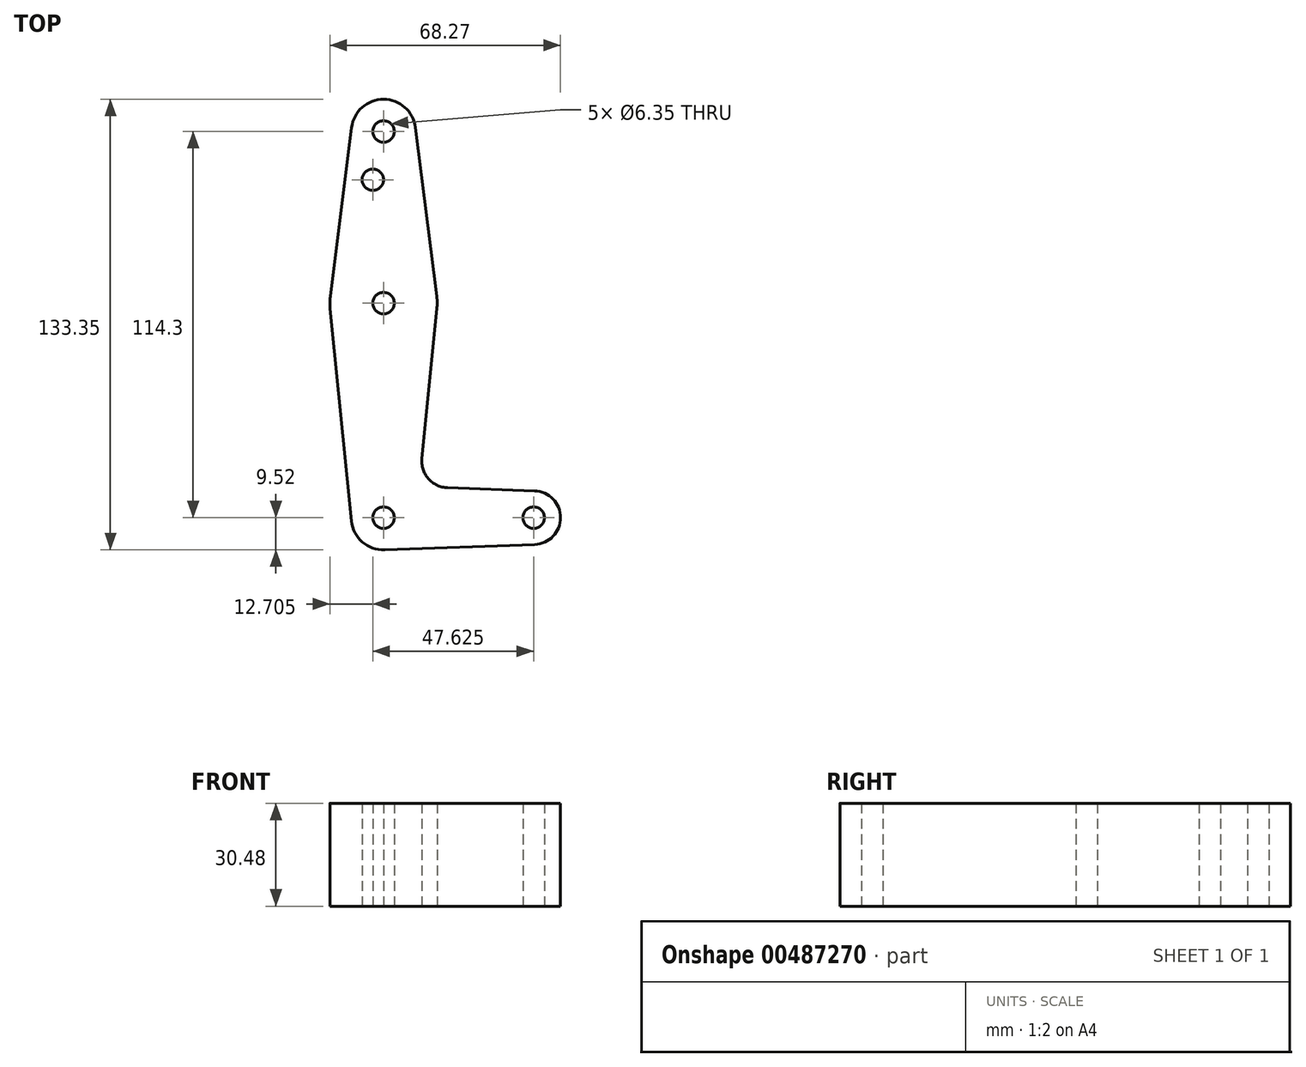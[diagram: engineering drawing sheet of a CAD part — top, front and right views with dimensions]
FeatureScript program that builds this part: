
annotation { "Feature Type Name" : "Feature", "Feature Type Description" : "" }
export const myFeature = defineFeature(function(context is Context, id is Id, definition is map)
    precondition{}
    {
        {
            var Q0;
            Q0=qCreatedBy(makeId("Top.planeOp"),FACE);
            var sketch = newSketch(context, id + "F0", { "sketchPlane" : qUnion([Q0])});
            skLineSegment(sketch, "E0", {"start": v(0, 0) * mm, "end": v(0, 114.3) * mm, "construction": true});
            skLineSegment(sketch, "E1", {"start": v(0, 0) * mm, "end": v(44.45, 0) * mm, "construction": true});
            skCircle(sketch, "E2", {"center": v(0, 114.3) * mm, "radius": 9.52 * mm});
            skCircle(sketch, "E3", {"center": v(0, 0) * mm, "radius": 9.53 * mm});
            skCircle(sketch, "E4", {"center": v(44.45, 0) * mm, "radius": 7.94 * mm});
            skCircle(sketch, "E5", {"center": v(0, 63.5) * mm, "radius": 15.88 * mm});
            skLineSegment(sketch, "E6", {"start": v(9.45, 115.5) * mm, "end": v(15.75, 65.48) * mm});
            skLineSegment(sketch, "E7", {"start": v(-9.45, 115.5) * mm, "end": v(-15.75, 65.48) * mm});
            skLineSegment(sketch, "E8", {"start": v(15.8, 61.91) * mm, "end": v(11.34, 17.6) * mm});
            skLineSegment(sketch, "E9", {"start": v(-15.8, 61.91) * mm, "end": v(-9.48, -0.95) * mm});
            skLineSegment(sketch, "E10", {"start": v(18.97, 8.85) * mm, "end": v(44.73, 7.93) * mm});
            skLineSegment(sketch, "E11", {"start": v(0.34, -9.52) * mm, "end": v(44.73, -7.93) * mm});
            skCircle(sketch, "E12", {"center": v(0, 114.3) * mm, "radius": 3.18 * mm});
            skCircle(sketch, "E13", {"center": v(0, 63.5) * mm, "radius": 3.17 * mm});
            skCircle(sketch, "E14", {"center": v(0, 0) * mm, "radius": 3.18 * mm});
            skCircle(sketch, "E15", {"center": v(44.45, 0) * mm, "radius": 3.18 * mm});
            skCircle(sketch, "E16", {"center": v(-3.18, 100.03) * mm, "radius": 3.18 * mm});
            skArc(sketch, "E17.filletArc", {"start": v(11.34, 17.6) * mm, "mid": v(13.26, 11.57) * mm, "end": v(18.97, 8.85) * mm});
            skSolve(sketch);
        }
        {
            var Q0;
            Q0 = qSketchRegion(id + "F0", true);
            extrude(context, id + "F1", {"entities" : qUnion([Q0]), "depth" : 30.48 * mm});
        }
    });
